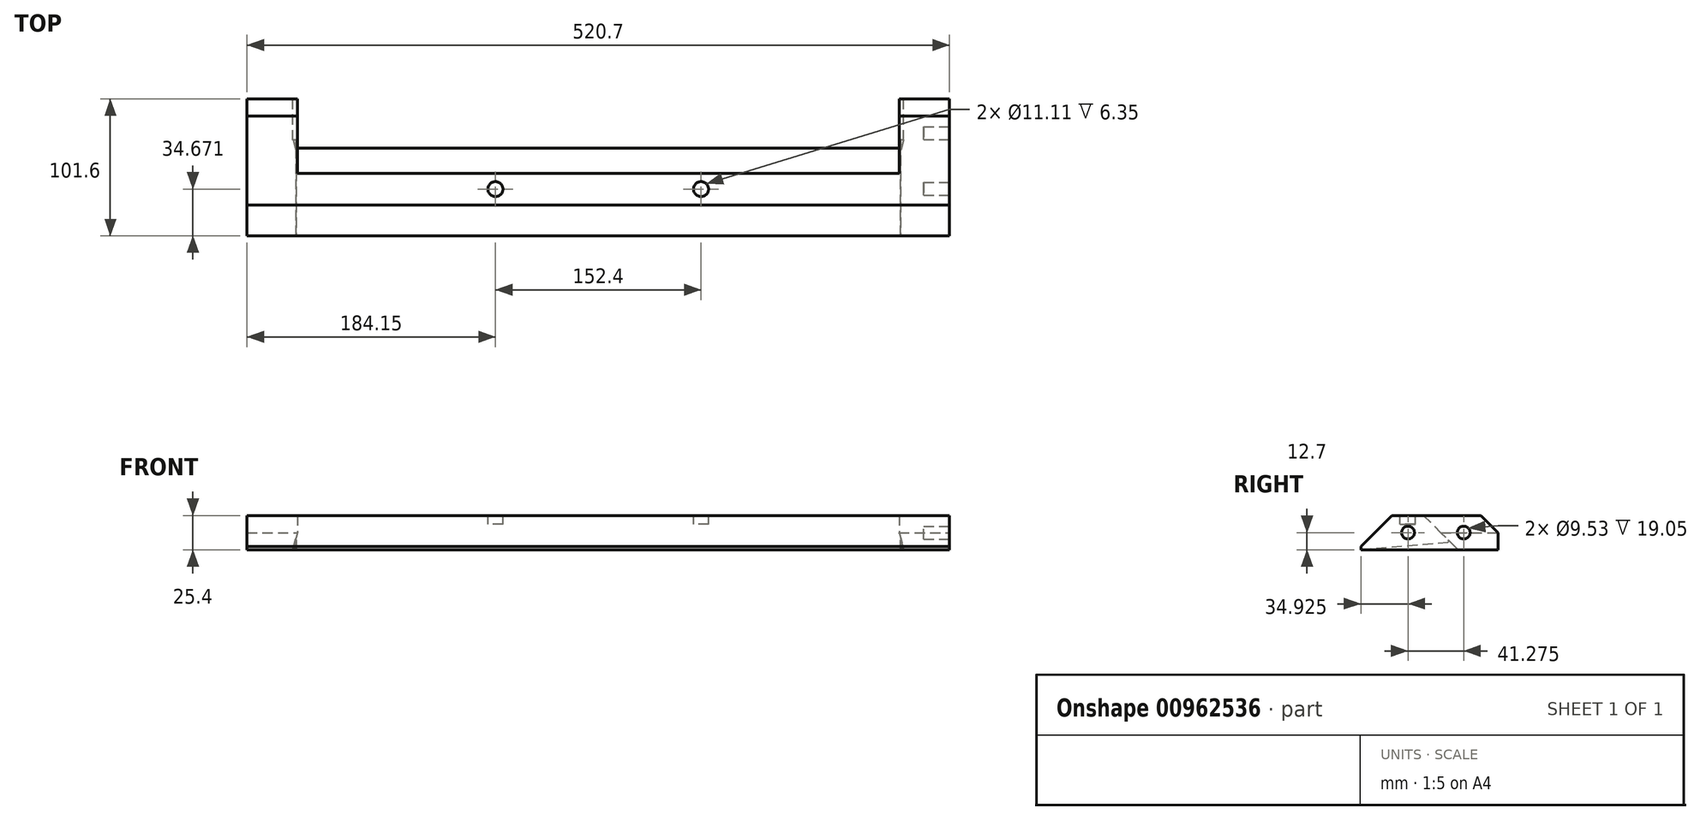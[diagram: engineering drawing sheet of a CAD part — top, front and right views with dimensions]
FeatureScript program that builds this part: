
annotation { "Feature Type Name" : "Feature", "Feature Type Description" : "" }
export const myFeature = defineFeature(function(context is Context, id is Id, definition is map)
    precondition{}
    {
        {
            var Q0;
            Q0=qCreatedBy(makeId("Top.planeOp"),FACE);
            var sketch = newSketch(context, id + "F0", { "sketchPlane" : qUnion([Q0])});
            skLineSegment(sketch, "E0", {"start": v(0, 0) * mm, "end": v(0, 249.49) * mm, "construction": true});
            skLineSegment(sketch, "E1.bottom", {"start": v(-260.35, 101.6) * mm, "end": v(260.35, 101.6) * mm});
            skLineSegment(sketch, "E1.top", {"start": v(-260.35, 0) * mm, "end": v(260.35, 0) * mm});
            skLineSegment(sketch, "E1.left", {"start": v(-260.35, 101.6) * mm, "end": v(-260.35, 0) * mm});
            skLineSegment(sketch, "E1.right", {"start": v(260.35, 101.6) * mm, "end": v(260.35, 0) * mm});
            skSolve(sketch);
        }
        {
            var Q0;
            Q0 = qSketchRegion(id + "F0", true);
            extrude(context, id + "F1", {"entities" : qUnion([Q0]), "depth" : 25.4 * mm, "offsetDistance" : 25.4 * mm});
        }
        {
            var Q0;
            Q0=makeQuery(id+"F1.opExtrude","CAP_EDGE",EDGE,{"disambiguationData":[OSD([sQuery(id+"F0.wireOp",EDGE,"E1.top")])],"isStart":false});
            chamfer(context, id + "F2", {"entities" : qUnion([Q0]), "width" : 22.86 * mm, "tangentPropagation" : true});
        }
        {
            var Q0;
            Q0=makeQuery(id+"F1.opExtrude","CAP_FACE",FACE,{"disambiguationData":[OSD([sQuery(id+"F0.wireOp",EDGE,"E1.bottom"),sQuery(id+"F0.wireOp",EDGE,"E1.top"),sQuery(id+"F0.wireOp",EDGE,"E1.left"),sQuery(id+"F0.wireOp",EDGE,"E1.right")])],"isStart":false});
            var sketch = newSketch(context, id + "F3", { "sketchPlane" : qUnion([Q0])});
            skLineSegment(sketch, "E2", {"start": v(0, 0) * mm, "end": v(0, 133.24) * mm, "construction": true});
            skLineSegment(sketch, "E3.bottom", {"start": v(-223.04, 101.6) * mm, "end": v(223.04, 101.6) * mm});
            skLineSegment(sketch, "E3.top", {"start": v(-223.04, 46.48) * mm, "end": v(223.04, 46.48) * mm});
            skLineSegment(sketch, "E3.left", {"start": v(-223.04, 101.6) * mm, "end": v(-223.04, 46.48) * mm});
            skLineSegment(sketch, "E3.right", {"start": v(223.04, 101.6) * mm, "end": v(223.04, 46.48) * mm});
            skSolve(sketch);
        }
        {
            var Q0;
            Q0 = qSketchRegion(id + "F3", true);
            extrude(context, id + "F4", {"entities" : qUnion([Q0]), "operationType" : NewBodyOperationType.REMOVE, "endBound" : BoundingType.THROUGH_ALL, "oppositeDirection" : true, "depth" : 25.4 * mm, "offsetDistance" : 25.4 * mm});
        }
        {
            var Q0;
            {var subQ0=sQuery(id+"F0.wireOp",EDGE,"E1.right");var subQ3=sQuery(id+"F0.wireOp",EDGE,"E1.bottom");Q0=makeQuery(id+"F4.boolean.opBoolean","SPLIT",FACE,{"disambiguationData":[TD([makeQuery(id+"F1.opExtrude","SWEPT_FACE",FACE,{"disambiguationData":[OSD([subQ0])]})])],"derivedFrom":makeQuery(id+"F1.opExtrude","SWEPT_FACE",FACE,{"disambiguationData":[OSD([subQ3])]})});}
            var sketch = newSketch(context, id + "F5", { "sketchPlane" : qUnion([Q0])});
            skLineSegment(sketch, "E4", {"start": v(0, 68.3) * mm, "end": v(0, -58.28) * mm, "construction": true});
            skLineSegment(sketch, "E5", {"start": v(-223.04, 12.7) * mm, "end": v(-226.44, 0) * mm});
            skLineSegment(sketch, "E6", {"start": v(-226.44, 0) * mm, "end": v(-223.04, 0) * mm});
            skLineSegment(sketch, "E7", {"start": v(-223.04, 0) * mm, "end": v(-223.04, 12.7) * mm});
            skLineSegment(sketch, "E8.MirrorCS", {"start": v(226.44, 0) * mm, "end": v(223.04, 0) * mm});
            skLineSegment(sketch, "E9.MirrorCS", {"start": v(223.04, 12.7) * mm, "end": v(226.44, 0) * mm});
            skLineSegment(sketch, "E10.MirrorCS", {"start": v(223.04, 0) * mm, "end": v(223.04, 12.7) * mm});
            skSolve(sketch);
        }
        {
            var Q0;
            Q0 = qSketchRegion(id + "F5", true);
            var Q1;
            Q1=makeQuery(id+"F4.boolean.opBoolean","COPY",FACE,{"derivedFrom":makeQuery(id+"F4.opExtrude","SWEPT_FACE",FACE,{"disambiguationData":[OSD([sQuery(id+"F3.wireOp",EDGE,"E3.top")])]})});
            extrude(context, id + "F6", {"entities" : qUnion([Q0]), "operationType" : NewBodyOperationType.REMOVE, "endBound" : BoundingType.UP_TO_SURFACE, "oppositeDirection" : true, "depth" : 38.1 * mm, "endBoundEntityFace" : qUnion([Q1]), "offsetDistance" : 25.4 * mm});
        }
        {
            var Q0;
            {var subQ0=sQuery(id+"F0.wireOp",EDGE,"E1.bottom");var subQ1=sQuery(id+"F0.wireOp",EDGE,"E1.right");Q0=makeQuery(id+"F4.boolean.opBoolean","SPLIT",EDGE,{"disambiguationData":[TD([makeQuery(id+"F1.opExtrude","SWEPT_FACE",FACE,{"disambiguationData":[OSD([subQ1])]})])],"derivedFrom":makeQuery(id+"F1.opExtrude","CAP_EDGE",EDGE,{"disambiguationData":[OSD([subQ0])],"isStart":false})});}
            var Q1;
            {var subQ0=sQuery(id+"F0.wireOp",EDGE,"E1.bottom");var subQ1=sQuery(id+"F0.wireOp",EDGE,"E1.left");Q1=makeQuery(id+"F4.boolean.opBoolean","SPLIT",EDGE,{"disambiguationData":[TD([makeQuery(id+"F1.opExtrude","SWEPT_FACE",FACE,{"disambiguationData":[OSD([subQ1])]})])],"derivedFrom":makeQuery(id+"F1.opExtrude","CAP_EDGE",EDGE,{"disambiguationData":[OSD([subQ0])],"isStart":false})});}
            chamfer(context, id + "F7", {"entities" : qUnion([Q0, Q1]), "width" : 12.7 * mm, "tangentPropagation" : true});
        }
        {
            var Q0;
            Q0=qCreatedBy(makeId("Right.planeOp"),FACE);
            var sketch = newSketch(context, id + "F8", { "sketchPlane" : qUnion([Q0])});
            skPoint(sketch, "E11", {"position": v(46.48, 25.4) * mm});
            skLineSegment(sketch, "E12", {"start": v(46.48, 25.4) * mm, "end": v(71.07, 0.81) * mm});
            skLineSegment(sketch, "E13", {"start": v(71.07, 0.81) * mm, "end": v(71.07, 0) * mm});
            skLineSegment(sketch, "E14", {"start": v(71.07, 0) * mm, "end": v(46.48, 0) * mm});
            skLineSegment(sketch, "E15", {"start": v(46.48, 0) * mm, "end": v(46.48, 25.4) * mm});
            skSolve(sketch);
        }
        {
            var Q0;
            Q0 = qSketchRegion(id + "F8", true);
            extrude(context, id + "F9", {"entities" : qUnion([Q0]), "operationType" : NewBodyOperationType.ADD, "endBound" : BoundingType.SYMMETRIC, "depth" : 457.2 * mm, "offsetDistance" : 25.4 * mm});
        }
        {
            var Q0;
            Q0=makeQuery(id+"F1.opExtrude","CAP_FACE",FACE,{"disambiguationData":[OSD([sQuery(id+"F0.wireOp",EDGE,"E1.bottom"),sQuery(id+"F0.wireOp",EDGE,"E1.top"),sQuery(id+"F0.wireOp",EDGE,"E1.left"),sQuery(id+"F0.wireOp",EDGE,"E1.right")])],"isStart":false});
            var sketch = newSketch(context, id + "F10", { "sketchPlane" : qUnion([Q0])});
            skLineSegment(sketch, "E16", {"start": v(0, 87.88) * mm, "end": v(0, 0) * mm, "construction": true});
            skCircle(sketch, "E17", {"center": v(76.2, 34.67) * mm, "radius": 5.56 * mm});
            skCircle(sketch, "E18.MirrorC", {"center": v(-76.2, 34.67) * mm, "radius": 5.56 * mm});
            skSolve(sketch);
        }
        {
            var Q0;
            Q0 = qSketchRegion(id + "F10", true);
            extrude(context, id + "F11", {"entities" : qUnion([Q0]), "operationType" : NewBodyOperationType.REMOVE, "oppositeDirection" : true, "depth" : 6.35 * mm, "offsetDistance" : 25.4 * mm});
        }
        {
            var Q0;
            Q0=makeQuery(id+"F1.opExtrude","SWEPT_FACE",FACE,{"disambiguationData":[OSD([sQuery(id+"F0.wireOp",EDGE,"E1.right")])]});
            var sketch = newSketch(context, id + "F12", { "sketchPlane" : qUnion([Q0])});
            skCircle(sketch, "E19", {"center": v(34.92, 12.7) * mm, "radius": 4.76 * mm});
            skCircle(sketch, "E20", {"center": v(76.2, 12.7) * mm, "radius": 4.76 * mm});
            skSolve(sketch);
        }
        {
            var Q0;
            Q0 = qSketchRegion(id + "F12", true);
            extrude(context, id + "F13", {"entities" : qUnion([Q0]), "operationType" : NewBodyOperationType.REMOVE, "oppositeDirection" : true, "depth" : 19.05 * mm, "offsetDistance" : 25.4 * mm});
        }
        {
            var Q0;
            Q0=qCreatedBy(makeId("Right.planeOp"),FACE);
            var sketch = newSketch(context, id + "F14", { "sketchPlane" : qUnion([Q0])});
            skLineSegment(sketch, "E21", {"start": v(0, 0) * mm, "end": v(106.96, 9.36) * mm});
            skLineSegment(sketch, "E22", {"start": v(106.96, 9.36) * mm, "end": v(107.78, 0) * mm});
            skLineSegment(sketch, "E23", {"start": v(107.78, 0) * mm, "end": v(0, 0) * mm});
            skSolve(sketch);
        }
        {
            var Q0;
            Q0 = qSketchRegion(id + "F14", true);
            extrude(context, id + "F15", {"entities" : qUnion([Q0]), "operationType" : NewBodyOperationType.REMOVE, "endBound" : BoundingType.SYMMETRIC, "oppositeDirection" : true, "depth" : 448.06 * mm, "offsetDistance" : 25.4 * mm});
        }
        {
            var Q0;
            Q0=makeQuery(id+"F15.boolean.opBoolean","INTERSECT",EDGE,{"derivedFrom":[makeQuery(id+"F9.opExtrude","SWEPT_FACE",FACE,{"disambiguationData":[OSD([sQuery(id+"F8.wireOp",EDGE,"E12")])]}),makeQuery(id+"F15.opExtrude","SWEPT_FACE",FACE,{"disambiguationData":[OSD([sQuery(id+"F14.wireOp",EDGE,"E21")])]})]});
            fillet(context, id + "F16", {"entities" : qUnion([Q0]), "radius" : 0.82 * mm, "tangentPropagation" : true, "allowEdgeOverflow" : false});
        }
    });
